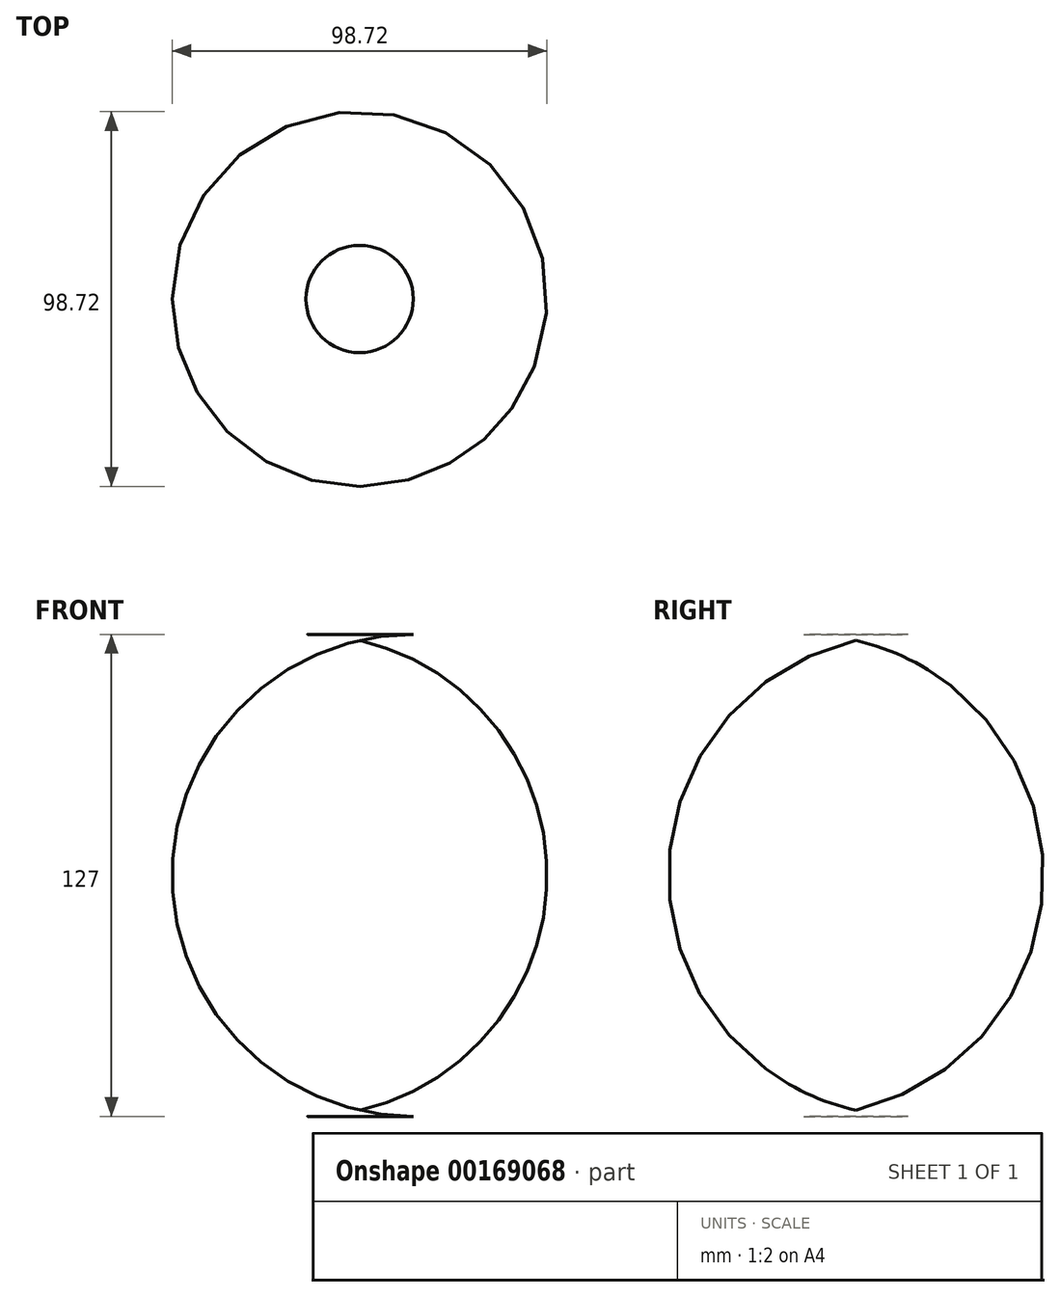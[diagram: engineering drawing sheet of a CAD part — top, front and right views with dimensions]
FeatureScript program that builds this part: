
annotation { "Feature Type Name" : "Feature", "Feature Type Description" : "" }
export const myFeature = defineFeature(function(context is Context, id is Id, definition is map)
    precondition{}
    {
        {
            var Q0;
            Q0=qCreatedBy(makeId("Top.planeOp"),FACE);
            var sketch = newSketch(context, id + "F0", { "sketchPlane" : qUnion([Q0])});
            skCircle(sketch, "E0", {"center": v(0, 0) * mm, "radius": 50.8 * mm});
            skSolve(sketch);
        }
        {
            var Q0;
            Q0=makeQuery(id+"F0.imprint","IMPRINT",FACE,{"disambiguationData":[TD([[makeQuery(id+"F0.imprint","IMPRINT",EDGE,{"derivedFrom":sQuery(id+"F0.wireOp",EDGE,"E0")}),1.0]])]});
            extrude(context, id + "F1", {"entities" : qUnion([Q0]), "depth" : 63.5 * mm, "hasDraft" : true, "draftAngle" : 30 * degree});
        }
        {
            var Q0;
            Q0=makeQuery(id+"F1.opExtrude","CAP_FACE",FACE,{"disambiguationData":[OSD([sQuery(id+"F0.wireOp",EDGE,"E0")])],"isStart":false});
            extrude(context, id + "F2", {"entities" : qUnion([Q0]), "operationType" : NewBodyOperationType.ADD, "depth" : 63.5 * mm, "hasDraft" : true, "draftAngle" : 30 * degree, "draftPullDirection" : true});
        }
        {
            var Q0;
            {var subQ0=sQuery(id+"F0.wireOp",EDGE,"E0");Q0=makeQuery(id+"F2.boolean.opBoolean","MERGE",EDGE,{"derivedFrom":[makeQuery(id+"F1.opExtrude","CAP_EDGE",EDGE,{"disambiguationData":[OSD([subQ0])],"isStart":false}),makeQuery(id+"F2.opExtrude","CAP_EDGE",EDGE,{"disambiguationData":[OSD([subQ0])],"isStart":true})]});}
            var Q1;
            Q1=makeQuery(id+"F2.opExtrude","CAP_EDGE",EDGE,{"disambiguationData":[OSD([sQuery(id+"F0.wireOp",EDGE,"E0")])],"isStart":false});
            var Q2;
            Q2=makeQuery(id+"F1.opExtrude","CAP_EDGE",EDGE,{"disambiguationData":[OSD([sQuery(id+"F0.wireOp",EDGE,"E0")])],"isStart":true});
            fillet(context, id + "F3", {"entities" : qUnion([Q0, Q1, Q2]), "radius" : 63.5 * mm, "tangentPropagation" : true, "allowEdgeOverflow" : false});
        }
    });
